# Revit family: GPB-400
name_source: partatom
category: Generic Models
revit_build: Autodesk Revit LT 2016 (Build: 20161004_0715(x64)
units: mm (PartAtom-declared; Revit-internal decimal feet)

## family parameters
Always vertical = Yes
Can host rebar = No
Cut with Voids When Loaded = No
Part Type = Normal
Room Calculation Point = No
Round Connector Dimension = Use Diameter
Shared = No
Work Plane-Based = No

## types (1)
- GPB-400
    A = 10.61 "
    B = 5.44 "
    BLADE = AA-610-325
    C = 12.38 "
    D = 6 "
    F = 8.5 "
    G = 11.12 "
    H = 5.12 "
    HOUSING = #1061  M=5.25
    J = 6 "
    K = 3.75 "
    MOTOR = CA2F080N
    Manufacturer = REVERSOMATIC
    Model = GPB-400
    RPM = 1500
    SP/CFM = .00/403  .05/394  .10/368  .15/378  .20/370  .25/362  .30/357  .35/349  .40/344  .45/335  .50/326  .55/317  .60/302  .65/287  .70/265  .75/240
    URL = http://www.reversomatic.com

## geometry (parser evidence)
native form markers: Sweep x2
no freeform markers — native parametric forms only
